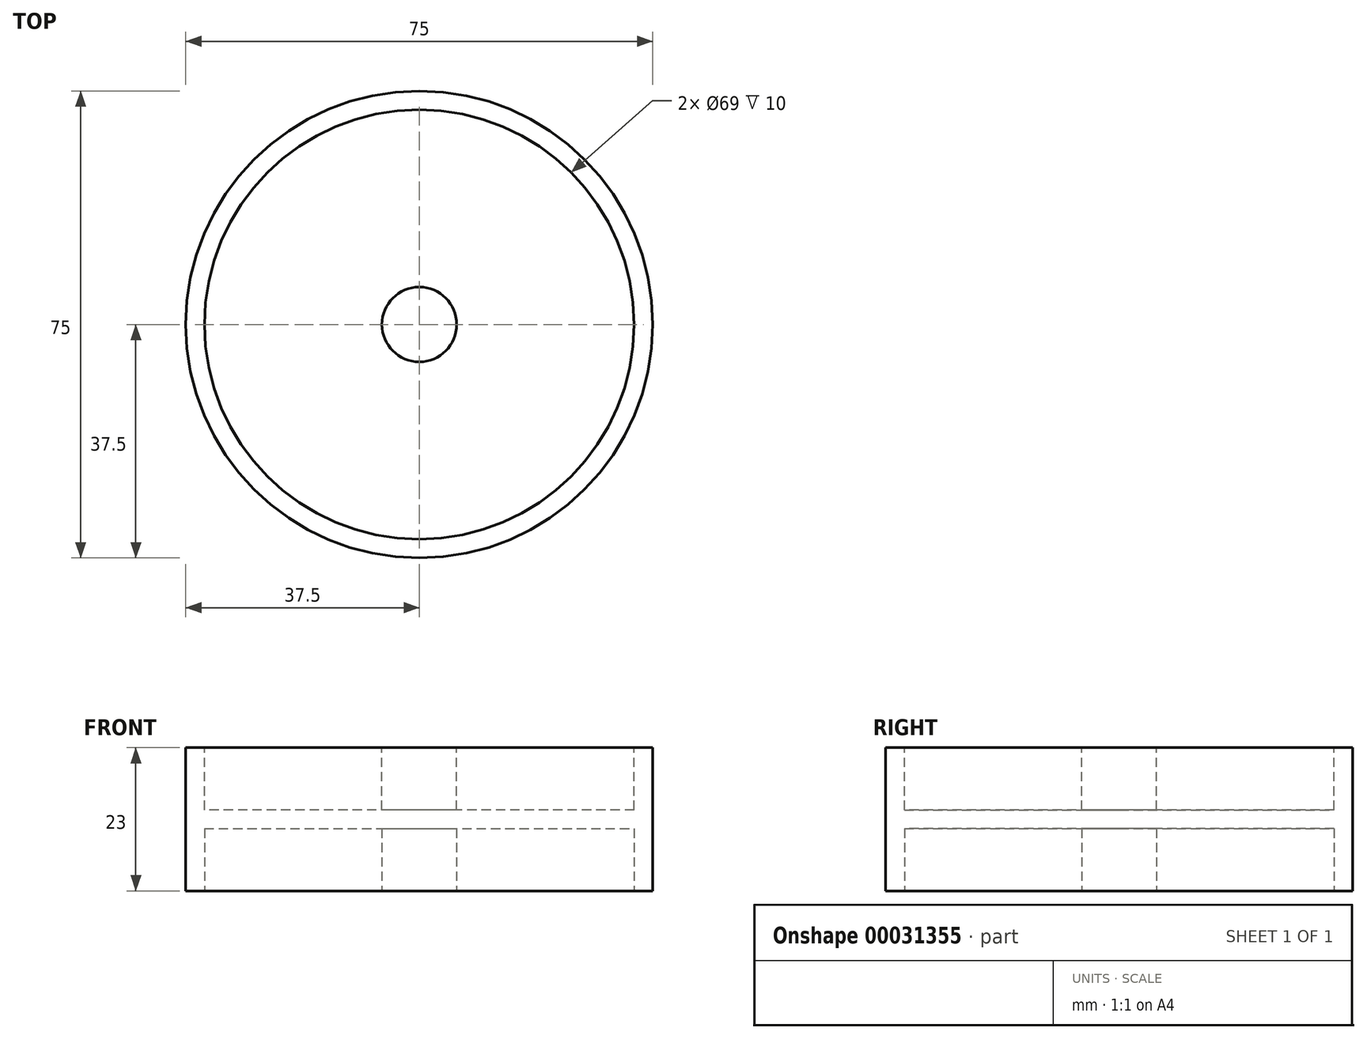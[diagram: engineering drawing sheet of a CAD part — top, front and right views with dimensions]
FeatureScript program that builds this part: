
annotation { "Feature Type Name" : "Feature", "Feature Type Description" : "" }
export const myFeature = defineFeature(function(context is Context, id is Id, definition is map)
    precondition{}
    {
        {
            var Q0;
            Q0=qCreatedBy(makeId("Top.planeOp"),FACE);
            var sketch = newSketch(context, id + "F0", { "sketchPlane" : qUnion([Q0])});
            skCircle(sketch, "E0", {"center": v(0, 0) * mm, "radius": 37.5 * mm});
            skSolve(sketch);
        }
        {
            var Q0;
            Q0 = qSketchRegion(id + "F0", true);
            extrude(context, id + "F1", {"entities" : qUnion([Q0]), "depth" : 23 * mm});
        }
        {
            var Q0;
            Q0=makeQuery(id+"F1.opExtrude","CAP_FACE",FACE,{"disambiguationData":[OSD([sQuery(id+"F0.wireOp",EDGE,"E0")])],"isStart":false});
            var sketch = newSketch(context, id + "F2", { "sketchPlane" : qUnion([Q0])});
            skCircle(sketch, "E1", {"center": v(0, 0) * mm, "radius": 34.5 * mm});
            skCircle(sketch, "E2", {"center": v(0, 0) * mm, "radius": 6 * mm});
            skSolve(sketch);
        }
        {
            var Q0;
            Q0 = qSketchRegion(id + "F2", true);
            extrude(context, id + "F3", {"entities" : qUnion([Q0]), "operationType" : NewBodyOperationType.REMOVE, "oppositeDirection" : true, "depth" : 10 * mm});
        }
        {
            var Q0;
            Q0=makeQuery(id+"F1.opExtrude","CAP_FACE",FACE,{"disambiguationData":[OSD([sQuery(id+"F0.wireOp",EDGE,"E0")])],"isStart":true});
            var sketch = newSketch(context, id + "F4", { "sketchPlane" : qUnion([Q0])});
            skCircle(sketch, "E3", {"center": v(0, 0) * mm, "radius": 34.5 * mm});
            skCircle(sketch, "E4", {"center": v(0, 0) * mm, "radius": 6 * mm});
            skSolve(sketch);
        }
        {
            var Q0;
            Q0 = qSketchRegion(id + "F4", true);
            extrude(context, id + "F5", {"entities" : qUnion([Q0]), "operationType" : NewBodyOperationType.REMOVE, "oppositeDirection" : true, "depth" : 10 * mm});
        }
    });
